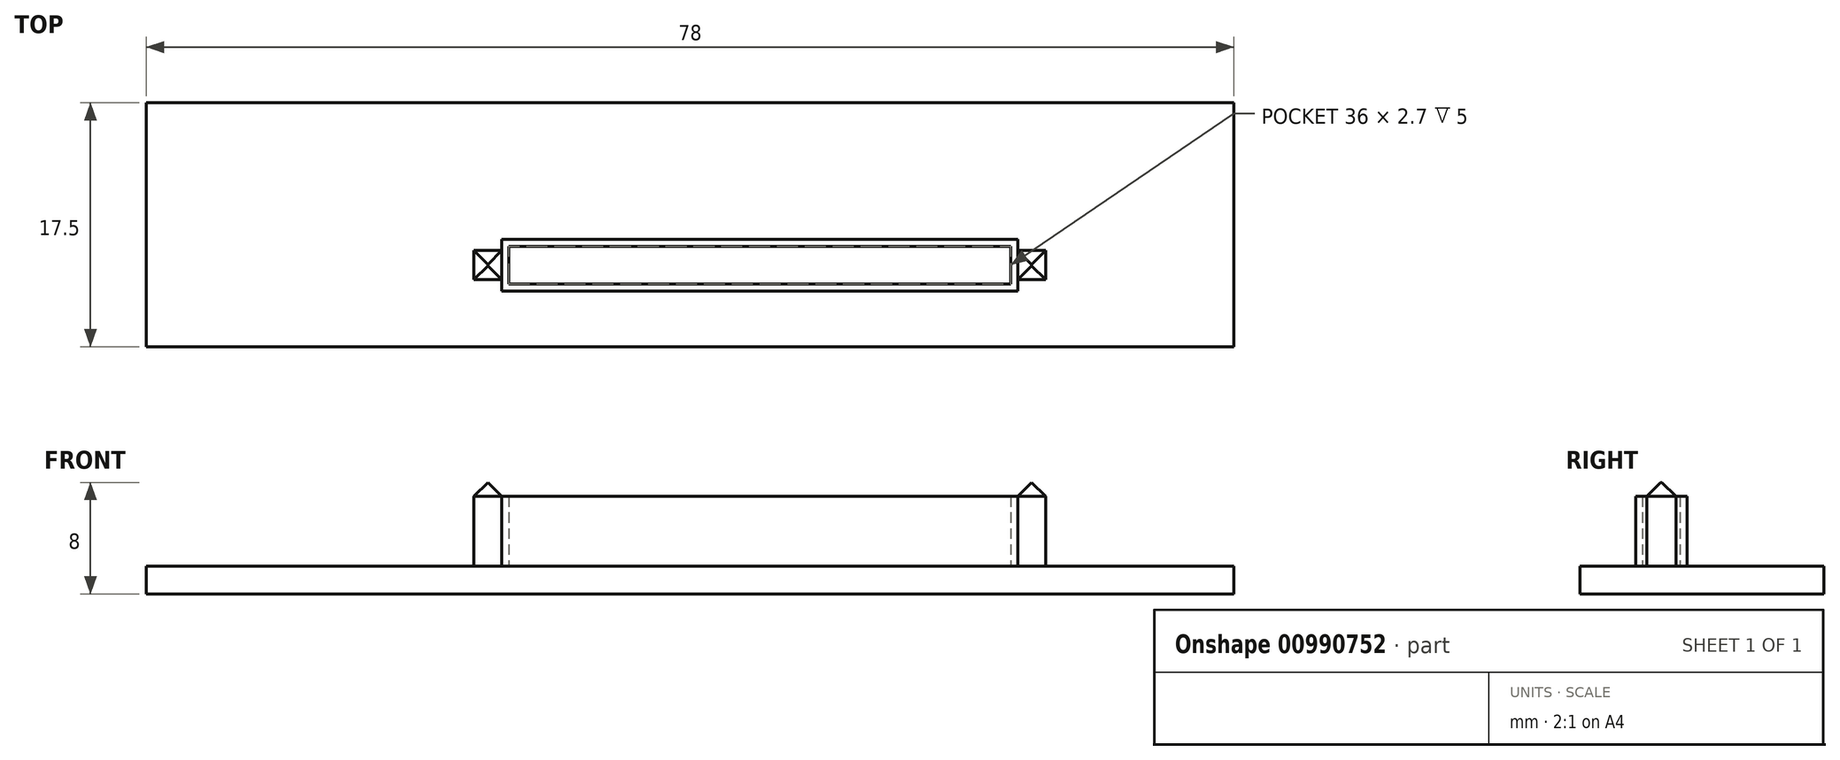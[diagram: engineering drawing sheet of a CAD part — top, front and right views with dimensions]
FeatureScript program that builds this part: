
annotation { "Feature Type Name" : "Feature", "Feature Type Description" : "" }
export const myFeature = defineFeature(function(context is Context, id is Id, definition is map)
    precondition{}
    {
        {
            var Q0;
            Q0=qCreatedBy(makeId("Top.planeOp"),FACE);
            var sketch = newSketch(context, id + "F0", { "sketchPlane" : qUnion([Q0])});
            skLineSegment(sketch, "E0.bottom", {"start": v(-39, 8.75) * mm, "end": v(39, 8.75) * mm});
            skLineSegment(sketch, "E0.top", {"start": v(-39, -8.75) * mm, "end": v(39, -8.75) * mm});
            skLineSegment(sketch, "E0.left", {"start": v(-39, 8.75) * mm, "end": v(-39, -8.75) * mm});
            skLineSegment(sketch, "E0.right", {"start": v(39, 8.75) * mm, "end": v(39, -8.75) * mm});
            skLineSegment(sketch, "E1.bottom", {"start": v(-35, 4.75) * mm, "end": v(35, 4.75) * mm, "construction": true});
            skLineSegment(sketch, "E1.top", {"start": v(-35, -4.75) * mm, "end": v(35, -4.75) * mm, "construction": true});
            skLineSegment(sketch, "E1.left", {"start": v(-35, 4.75) * mm, "end": v(-35, -4.75) * mm, "construction": true});
            skLineSegment(sketch, "E1.right", {"start": v(35, 4.75) * mm, "end": v(35, -4.75) * mm, "construction": true});
            skSolve(sketch);
        }
        {
            var Q0;
            Q0 = qSketchRegion(id + "F0", true);
            extrude(context, id + "F1", {"entities" : qUnion([Q0]), "depth" : 2 * mm, "offsetDistance" : 25 * mm});
        }
        {
            var Q0;
            Q0=makeQuery(id+"F1.opExtrude","CAP_FACE",FACE,{"disambiguationData":[OSD([sQuery(id+"F0.wireOp",EDGE,"E0.bottom"),sQuery(id+"F0.wireOp",EDGE,"E0.top"),sQuery(id+"F0.wireOp",EDGE,"E0.left"),sQuery(id+"F0.wireOp",EDGE,"E0.right")])],"isStart":false});
            var sketch = newSketch(context, id + "F2", { "sketchPlane" : qUnion([Q0])});
            skLineSegment(sketch, "E2.bottom", {"start": v(-35, 4.75) * mm, "end": v(35, 4.75) * mm});
            skLineSegment(sketch, "E2.top", {"start": v(-35, -4.75) * mm, "end": v(35, -4.75) * mm});
            skLineSegment(sketch, "E2.left", {"start": v(-35, 4.75) * mm, "end": v(-35, -4.75) * mm});
            skLineSegment(sketch, "E2.right", {"start": v(35, 4.75) * mm, "end": v(35, -4.75) * mm});
            skLineSegment(sketch, "E3.bottom", {"start": v(-39, 8.75) * mm, "end": v(39, 8.75) * mm});
            skLineSegment(sketch, "E3.top", {"start": v(-39, -8.75) * mm, "end": v(39, -8.75) * mm});
            skLineSegment(sketch, "E3.left", {"start": v(-39, 8.75) * mm, "end": v(-39, -8.75) * mm});
            skLineSegment(sketch, "E3.right", {"start": v(39, 8.75) * mm, "end": v(39, -8.75) * mm});
            skLineSegment(sketch, "E4.bottom", {"start": v(23.5, -4.75) * mm, "end": v(-13.5, -4.75) * mm});
            skLineSegment(sketch, "E4.top", {"start": v(23.5, -1.05) * mm, "end": v(-13.5, -1.05) * mm});
            skLineSegment(sketch, "E4.left", {"start": v(23.5, -4.75) * mm, "end": v(23.5, -1.05) * mm});
            skLineSegment(sketch, "E4.right", {"start": v(-13.5, -4.75) * mm, "end": v(-13.5, -1.05) * mm});
            skPoint(sketch, "E5.positionSnap0", {"position": v(5, -1.05) * mm});
            skPoint(sketch, "E6", {"position": v(-13.5, -2.9) * mm});
            skLineSegment(sketch, "E7", {"start": v(5, -1.05) * mm, "end": v(5, -4.75) * mm, "construction": true});
            skLineSegment(sketch, "E8", {"start": v(-13.5, -2.9) * mm, "end": v(23.5, -2.9) * mm, "construction": true});
            skPoint(sketch, "E9", {"position": v(5, -2.9) * mm});
            skLineSegment(sketch, "E10.bottom", {"start": v(23.5, -1.85) * mm, "end": v(25.5, -1.85) * mm});
            skLineSegment(sketch, "E10.top", {"start": v(23.5, -3.95) * mm, "end": v(25.5, -3.95) * mm});
            skLineSegment(sketch, "E10.left", {"start": v(23.5, -1.85) * mm, "end": v(23.5, -3.95) * mm});
            skLineSegment(sketch, "E10.right", {"start": v(25.5, -1.85) * mm, "end": v(25.5, -3.95) * mm});
            skLineSegment(sketch, "E11.MirrorCS", {"start": v(-13.5, -1.85) * mm, "end": v(-15.5, -1.85) * mm});
            skLineSegment(sketch, "E12.MirrorCS", {"start": v(-13.5, -3.95) * mm, "end": v(-15.5, -3.95) * mm});
            skLineSegment(sketch, "E13.MirrorCS", {"start": v(-15.5, -1.85) * mm, "end": v(-15.5, -3.95) * mm});
            skLineSegment(sketch, "E14.MirrorCS", {"start": v(-13.5, -1.85) * mm, "end": v(-13.5, -3.95) * mm});
            skLineSegment(sketch, "E15.bottom", {"start": v(-13, -1.55) * mm, "end": v(23, -1.55) * mm});
            skLineSegment(sketch, "E15.top", {"start": v(-13, -4.25) * mm, "end": v(23, -4.25) * mm});
            skLineSegment(sketch, "E15.left", {"start": v(-13, -1.55) * mm, "end": v(-13, -4.25) * mm});
            skLineSegment(sketch, "E15.right", {"start": v(23, -1.55) * mm, "end": v(23, -4.25) * mm});
            skSolve(sketch);
        }
        {
            var Q0;
            {var subQ4=sQuery(id+"F2.wireOp",EDGE,"E4.top");Q0=makeQuery(id+"F2.imprint","IMPRINT",FACE,{"disambiguationData":[TD([[makeQuery(id+"F2.imprint","IMPRINT",EDGE,{"derivedFrom":subQ4}),1.0]])]});}
            var Q1;
            {var subQ2=sQuery(id+"F2.wireOp",EDGE,"E11.MirrorCS");Q1=makeQuery(id+"F2.imprint","IMPRINT",FACE,{"disambiguationData":[TD([[makeQuery(id+"F2.imprint","IMPRINT",EDGE,{"derivedFrom":subQ2}),1.0]])]});}
            var Q2;
            {var subQ2=sQuery(id+"F2.wireOp",EDGE,"E10.bottom");Q2=makeQuery(id+"F2.imprint","IMPRINT",FACE,{"disambiguationData":[TD([[makeQuery(id+"F2.imprint","IMPRINT",EDGE,{"derivedFrom":subQ2}),-1.0]])]});}
            extrude(context, id + "F3", {"entities" : qUnion([Q0, Q1, Q2]), "operationType" : NewBodyOperationType.ADD, "depth" : 5 * mm, "offsetDistance" : 25 * mm});
        }
        {
            var Q0;
            Q0=makeQuery(id+"F3.opExtrude","CAP_FACE",FACE,{"disambiguationData":[OSD([sQuery(id+"F2.wireOp",EDGE,"E2.top"),sQuery(id+"F2.wireOp",EDGE,"E4.top"),sQuery(id+"F2.wireOp",EDGE,"E4.left"),sQuery(id+"F2.wireOp",EDGE,"E4.right"),sQuery(id+"F2.wireOp",EDGE,"E10.bottom"),sQuery(id+"F2.wireOp",EDGE,"E10.top"),sQuery(id+"F2.wireOp",EDGE,"E10.right"),sQuery(id+"F2.wireOp",EDGE,"E11.MirrorCS"),sQuery(id+"F2.wireOp",EDGE,"E12.MirrorCS"),sQuery(id+"F2.wireOp",EDGE,"E13.MirrorCS"),sQuery(id+"F2.wireOp",EDGE,"E15.bottom"),sQuery(id+"F2.wireOp",EDGE,"E15.top"),sQuery(id+"F2.wireOp",EDGE,"E15.left"),sQuery(id+"F2.wireOp",EDGE,"E15.right")])],"isStart":false});
            var sketch = newSketch(context, id + "F4", { "sketchPlane" : qUnion([Q0])});
            skLineSegment(sketch, "E16.bottom", {"start": v(-13.5, -1.85) * mm, "end": v(-15.5, -1.85) * mm});
            skLineSegment(sketch, "E16.top", {"start": v(-13.5, -3.95) * mm, "end": v(-15.5, -3.95) * mm});
            skLineSegment(sketch, "E16.left", {"start": v(-13.5, -1.85) * mm, "end": v(-13.5, -3.95) * mm});
            skLineSegment(sketch, "E16.right", {"start": v(-15.5, -1.85) * mm, "end": v(-15.5, -3.95) * mm});
            skLineSegment(sketch, "E17.bottom", {"start": v(23.5, -1.85) * mm, "end": v(25.5, -1.85) * mm});
            skLineSegment(sketch, "E17.top", {"start": v(23.5, -3.95) * mm, "end": v(25.5, -3.95) * mm});
            skLineSegment(sketch, "E17.left", {"start": v(23.5, -1.85) * mm, "end": v(23.5, -3.95) * mm});
            skLineSegment(sketch, "E17.right", {"start": v(25.5, -1.85) * mm, "end": v(25.5, -3.95) * mm});
            skSolve(sketch);
        }
        {
            var Q0;
            Q0=makeQuery(id+"F4.imprint","IMPRINT",FACE,{"disambiguationData":[TD([[makeQuery(id+"F4.imprint","IMPRINT",EDGE,{"derivedFrom":sQuery(id+"F4.wireOp",EDGE,"E16.bottom")}),1.0]])]});
            var Q1;
            Q1=makeQuery(id+"F4.imprint","IMPRINT",FACE,{"disambiguationData":[TD([[makeQuery(id+"F4.imprint","IMPRINT",EDGE,{"derivedFrom":sQuery(id+"F4.wireOp",EDGE,"E17.bottom")}),-1.0]])]});
            extrude(context, id + "F5", {"entities" : qUnion([Q0, Q1]), "operationType" : NewBodyOperationType.ADD, "depth" : 1 * mm, "offsetDistance" : 25 * mm});
        }
        {
            var Q0;
            Q0=makeQuery(id+"F5.opExtrude","CAP_EDGE",EDGE,{"disambiguationData":[OSD([sQuery(id+"F4.wireOp",EDGE,"E16.right")])],"isStart":false});
            var Q1;
            Q1=makeQuery(id+"F5.opExtrude","CAP_EDGE",EDGE,{"disambiguationData":[OSD([sQuery(id+"F4.wireOp",EDGE,"E16.bottom")])],"isStart":false});
            var Q2;
            Q2=makeQuery(id+"F5.opExtrude","CAP_EDGE",EDGE,{"disambiguationData":[OSD([sQuery(id+"F4.wireOp",EDGE,"E16.left")])],"isStart":false});
            var Q3;
            Q3=makeQuery(id+"F5.opExtrude","CAP_EDGE",EDGE,{"disambiguationData":[OSD([sQuery(id+"F4.wireOp",EDGE,"E16.top")])],"isStart":false});
            var Q4;
            Q4=makeQuery(id+"F5.opExtrude","CAP_EDGE",EDGE,{"disambiguationData":[OSD([sQuery(id+"F4.wireOp",EDGE,"E17.bottom")])],"isStart":false});
            var Q5;
            Q5=makeQuery(id+"F5.opExtrude","CAP_EDGE",EDGE,{"disambiguationData":[OSD([sQuery(id+"F4.wireOp",EDGE,"E17.left")])],"isStart":false});
            var Q6;
            Q6=makeQuery(id+"F5.opExtrude","CAP_EDGE",EDGE,{"disambiguationData":[OSD([sQuery(id+"F4.wireOp",EDGE,"E17.right")])],"isStart":false});
            var Q7;
            Q7=makeQuery(id+"F5.opExtrude","CAP_EDGE",EDGE,{"disambiguationData":[OSD([sQuery(id+"F4.wireOp",EDGE,"E17.top")])],"isStart":false});
            chamfer(context, id + "F6", {"entities" : qUnion([Q0, Q1, Q2, Q3, Q4, Q5, Q6, Q7]), "width" : 1 * mm, "tangentPropagation" : true});
        }
    });
